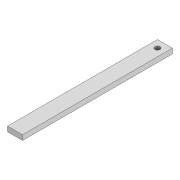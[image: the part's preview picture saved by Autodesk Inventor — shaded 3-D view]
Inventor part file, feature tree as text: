
AUTODESK INVENTOR PART (.ipt)
format: ipt  version: 2022 (Build 260153000, 153)  size: 79,872 bytes
history: native  units: mm
features: extrude x1, sketch x1
ambient origin geometry x8: Origin, YZ Plane, XZ Plane, XY Plane, X Axis, Y Axis, Z Axis, Center Point
bodies: Solid1 (feature_tree)
feature tree (2):
  extrude  "Extrusion1"  Depth=6.0mm
  sketch  "Sketch1"  dims[d0=60.0mm d1=6.0mm d2=2.0mm d4=2.0mm d5=3.0mm d6=2.0mm d7=0.0mm]
